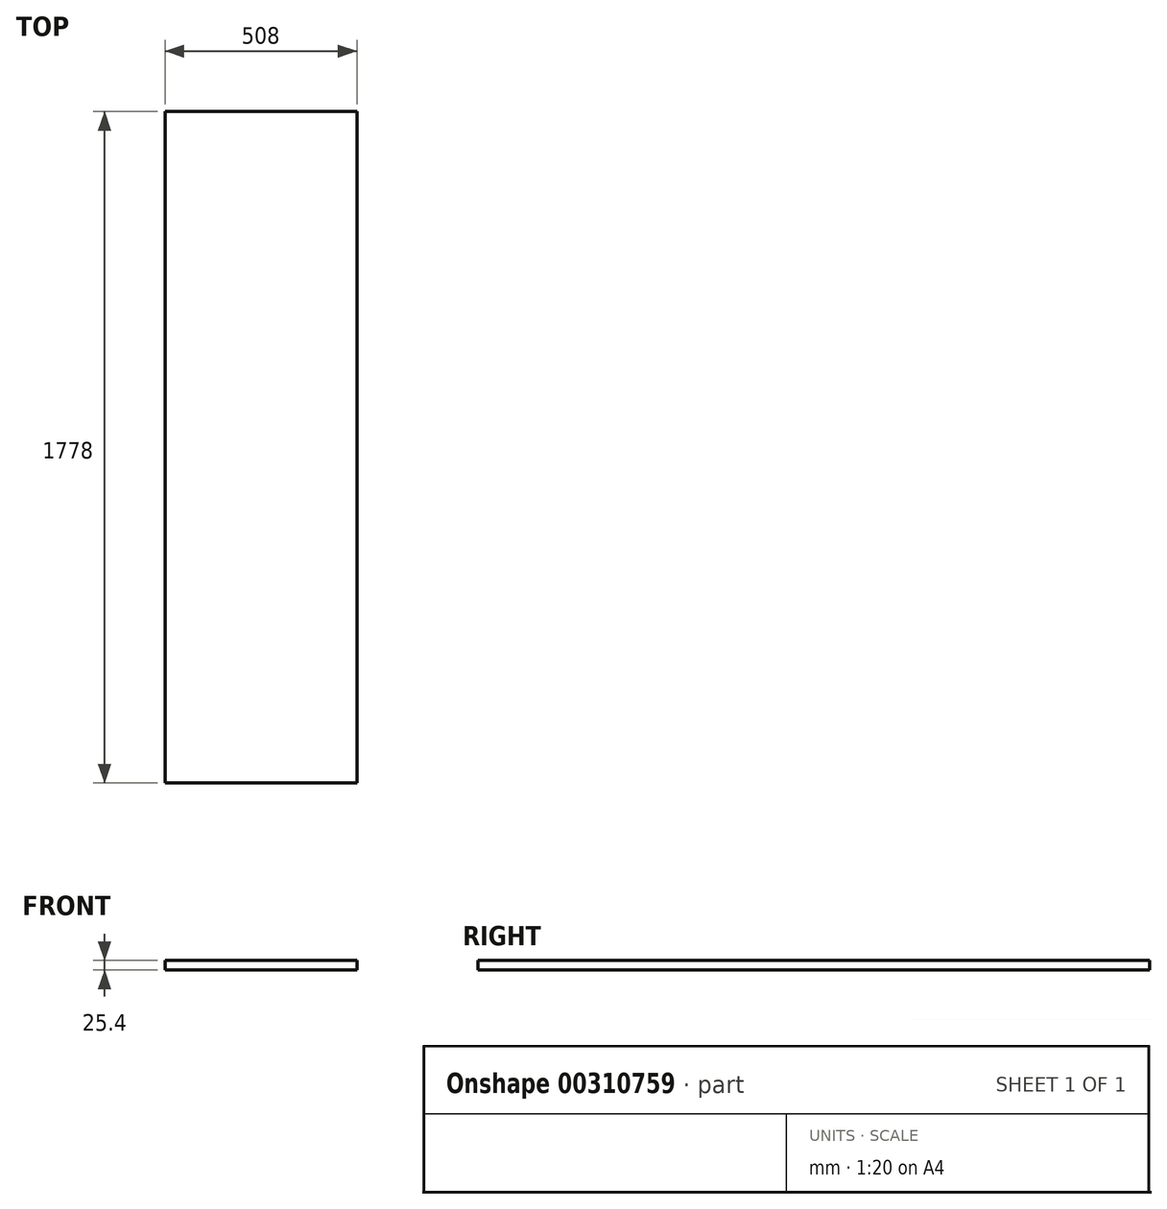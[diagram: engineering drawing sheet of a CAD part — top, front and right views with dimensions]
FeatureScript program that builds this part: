
annotation { "Feature Type Name" : "Feature", "Feature Type Description" : "" }
export const myFeature = defineFeature(function(context is Context, id is Id, definition is map)
    precondition{}
    {
        {
            var Q0;
            Q0=qCreatedBy(makeId("Top.planeOp"),FACE);
            var sketch = newSketch(context, id + "F0", { "sketchPlane" : qUnion([Q0])});
            skLineSegment(sketch, "E0.bottom", {"start": v(-43.49, 1716.12) * mm, "end": v(464.51, 1716.12) * mm});
            skLineSegment(sketch, "E0.top", {"start": v(-43.49, -61.88) * mm, "end": v(464.51, -61.88) * mm});
            skLineSegment(sketch, "E0.left", {"start": v(-43.49, 1716.12) * mm, "end": v(-43.49, -61.88) * mm});
            skLineSegment(sketch, "E0.right", {"start": v(464.51, 1716.12) * mm, "end": v(464.51, -61.88) * mm});
            skSolve(sketch);
        }
        {
            var Q0;
            Q0 = qSketchRegion(id + "F0", true);
            extrude(context, id + "F1", {"entities" : qUnion([Q0]), "oppositeDirection" : true, "depth" : 25.4 * mm, "offsetDistance" : 25.4 * mm});
        }
    });
